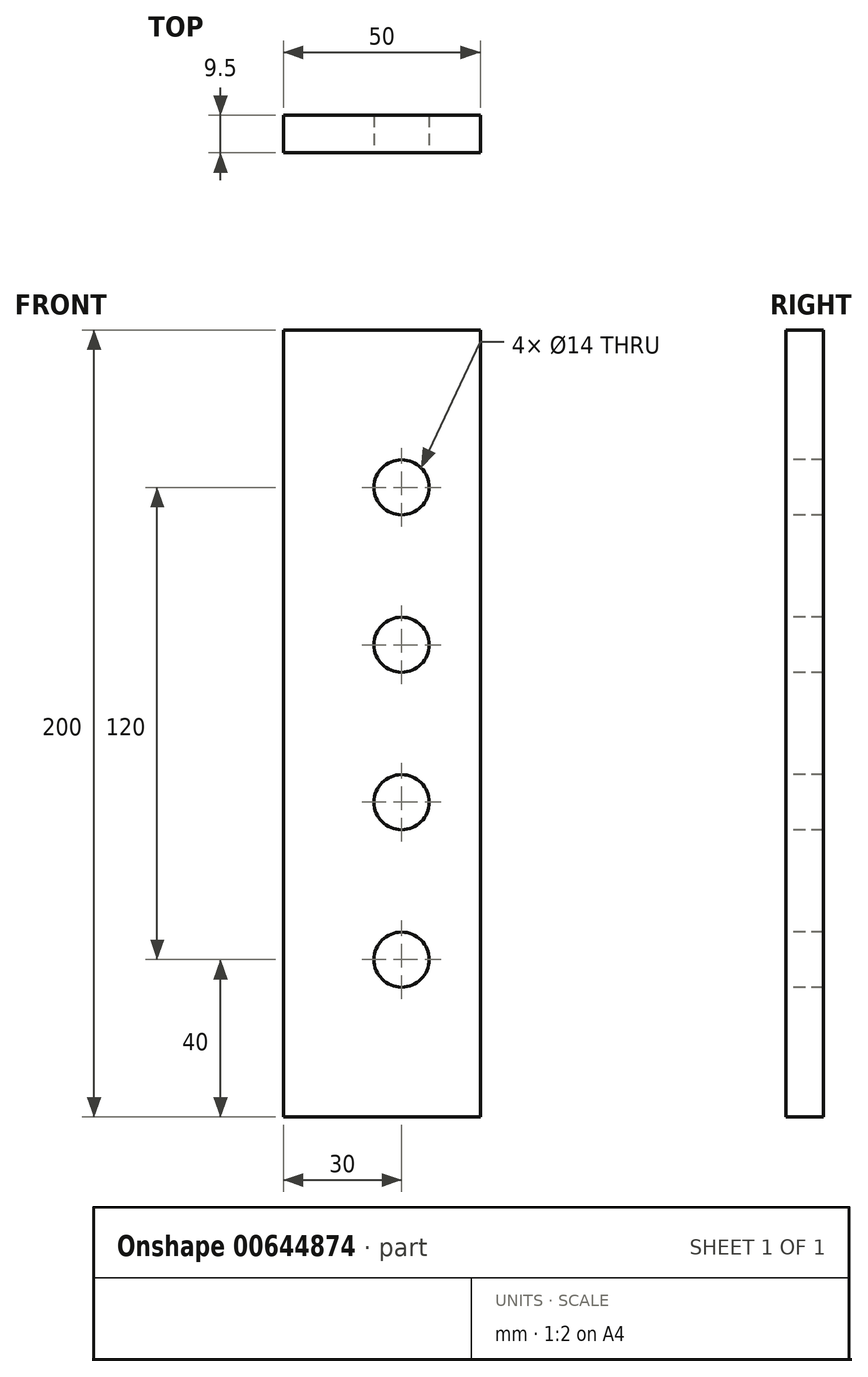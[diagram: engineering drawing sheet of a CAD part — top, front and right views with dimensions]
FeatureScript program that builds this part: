
annotation { "Feature Type Name" : "Feature", "Feature Type Description" : "" }
export const myFeature = defineFeature(function(context is Context, id is Id, definition is map)
    precondition{}
    {
        {
            var Q0;
            Q0=qCreatedBy(makeId("Front.planeOp"),FACE);
            var sketch = newSketch(context, id + "F0", { "sketchPlane" : qUnion([Q0])});
            skLineSegment(sketch, "E0.bottom", {"start": v(0, 0) * mm, "end": v(50, 0) * mm});
            skLineSegment(sketch, "E0.top", {"start": v(0, 200) * mm, "end": v(50, 200) * mm});
            skLineSegment(sketch, "E0.left", {"start": v(0, 0) * mm, "end": v(0, 200) * mm});
            skLineSegment(sketch, "E0.right", {"start": v(50, 0) * mm, "end": v(50, 200) * mm});
            skSolve(sketch);
        }
        {
            var Q0;
            Q0=makeQuery(id+"F0.imprint","IMPRINT",FACE,{"disambiguationData":[TD([[makeQuery(id+"F0.imprint","IMPRINT",EDGE,{"derivedFrom":sQuery(id+"F0.wireOp",EDGE,"E0.bottom")}),1.0]])]});
            extrude(context, id + "F1", {"entities" : qUnion([Q0]), "depth" : 9.5 * mm});
        }
        {
            var Q0;
            Q0=makeQuery(id+"F1.opExtrude","CAP_FACE",FACE,{"disambiguationData":[OSD([sQuery(id+"F0.wireOp",EDGE,"E0.bottom"),sQuery(id+"F0.wireOp",EDGE,"E0.top"),sQuery(id+"F0.wireOp",EDGE,"E0.left"),sQuery(id+"F0.wireOp",EDGE,"E0.right")])],"isStart":false});
            var sketch = newSketch(context, id + "F2", { "sketchPlane" : qUnion([Q0])});
            skLineSegment(sketch, "E1", {"start": v(30, 200) * mm, "end": v(30, 0) * mm});
            skPoint(sketch, "E2", {"position": v(30, 160) * mm});
            skPoint(sketch, "E3", {"position": v(30, 120) * mm});
            skPoint(sketch, "E4", {"position": v(30, 80) * mm});
            skPoint(sketch, "E5", {"position": v(30, 40) * mm});
            skSolve(sketch);
        }
        {
            var Q0;
            Q0=sQuery(id+"F2.wireOp",VERTEX,"E2");
            var Q1;
            Q1=sQuery(id+"F2.wireOp",VERTEX,"E3");
            var Q2;
            Q2=sQuery(id+"F2.wireOp",VERTEX,"E4");
            var Q3;
            Q3=sQuery(id+"F2.wireOp",VERTEX,"E5");
            var Q4;
            Q4=makeQuery(id+"F1.opExtrude","SWEPT_BODY",BODY,{"disambiguationData":[OSD([sQuery(id+"F0.wireOp",EDGE,"E0.bottom"),sQuery(id+"F0.wireOp",EDGE,"E0.top"),sQuery(id+"F0.wireOp",EDGE,"E0.left"),sQuery(id+"F0.wireOp",EDGE,"E0.right")])]});
            hole(context, id + "F3", {"style" : HoleStyle.SIMPLE, "endStyle" : HoleEndStyle.THROUGH, "holeDiameter" : 14 * mm, "tappedDepth" : 12 * mm, "tapClearance" : 3, "locations" : qUnion([Q0, Q1, Q2, Q3]), "scope" : qUnion([Q4])});
        }
    });
